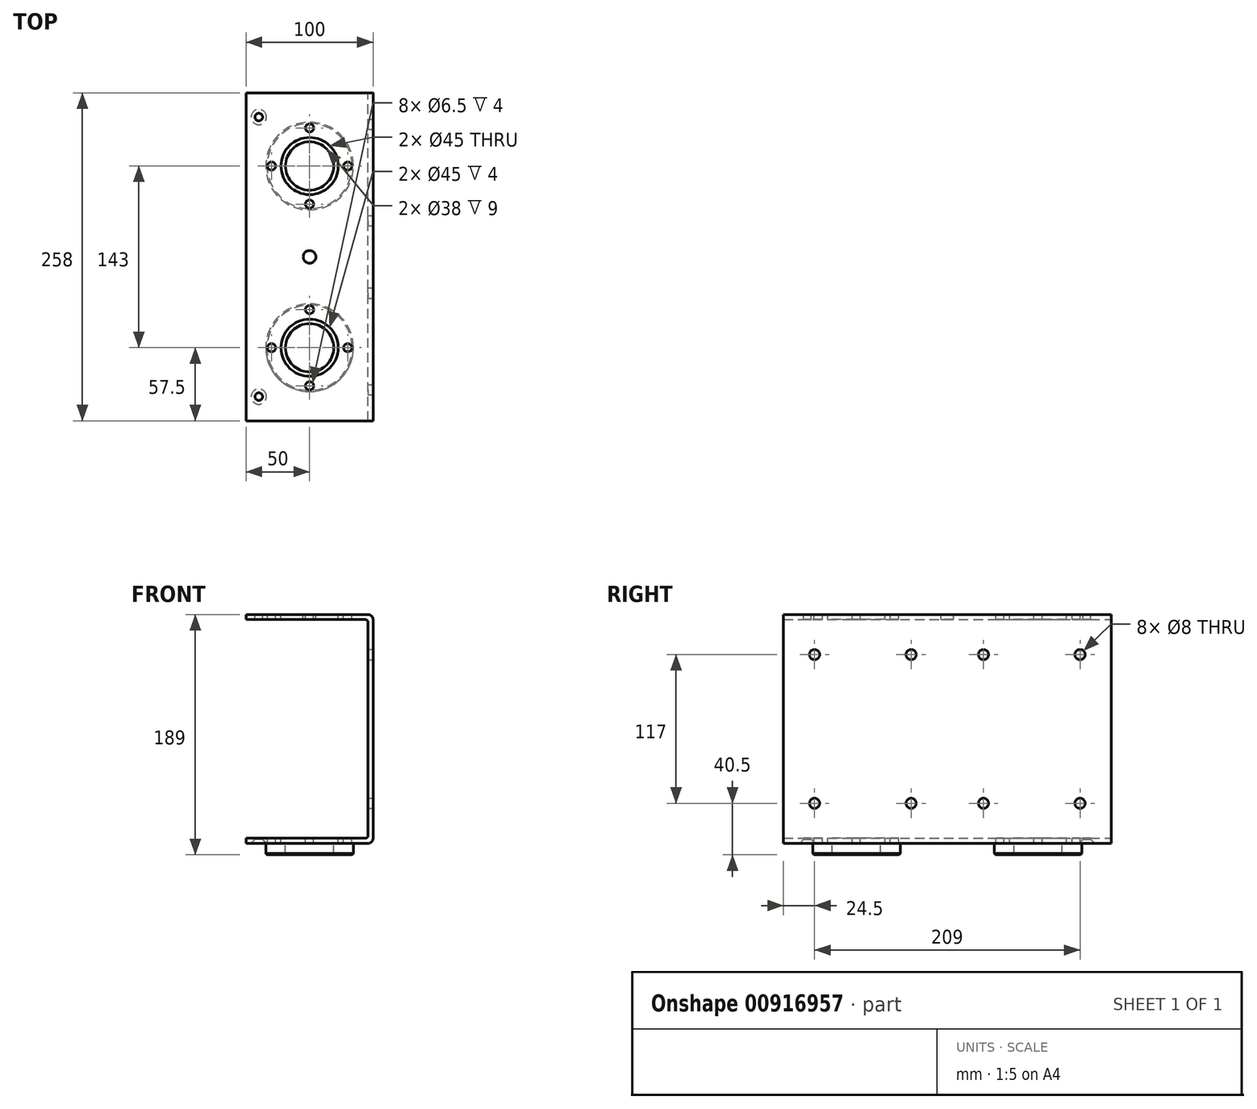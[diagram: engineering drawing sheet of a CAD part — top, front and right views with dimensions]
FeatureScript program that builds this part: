
annotation { "Feature Type Name" : "Feature", "Feature Type Description" : "" }
export const myFeature = defineFeature(function(context is Context, id is Id, definition is map)
    precondition{}
    {
        {
            var Q0;
            Q0=qCreatedBy(makeId("Front.planeOp"),FACE);
            var sketch = newSketch(context, id + "F0", { "sketchPlane" : qUnion([Q0])});
            skLineSegment(sketch, "E0.bottom", {"start": v(0, 0) * mm, "end": v(96, 0) * mm});
            skLineSegment(sketch, "E0.top", {"start": v(0, 180) * mm, "end": v(96, 180) * mm});
            skLineSegment(sketch, "E0.left", {"start": v(0, 0) * mm, "end": v(0, 4) * mm});
            skLineSegment(sketch, "E0.right", {"start": v(100, 4) * mm, "end": v(100, 176) * mm});
            skLineSegment(sketch, "E1.0", {"start": v(0, 176) * mm, "end": v(94, 176) * mm});
            skLineSegment(sketch, "E2.0", {"start": v(96, 6) * mm, "end": v(96, 174) * mm});
            skLineSegment(sketch, "E3.0", {"start": v(0, 4) * mm, "end": v(94, 4) * mm});
            skLineSegment(sketch, "E4.trimOffspring", {"start": v(0, 176) * mm, "end": v(0, 180) * mm});
            skPoint(sketch, "E5.visualSharp", {"position": v(100, 180) * mm});
            skArc(sketch, "E5.filletArc", {"start": v(100, 176) * mm, "mid": v(98.83, 178.83) * mm, "end": v(96, 180) * mm});
            skArc(sketch, "E6.filletArc", {"start": v(96, 174) * mm, "mid": v(95.41, 175.41) * mm, "end": v(94, 176) * mm});
            skPoint(sketch, "E7.visualSharp", {"position": v(96, 4) * mm});
            skArc(sketch, "E7.filletArc", {"start": v(94, 4) * mm, "mid": v(95.41, 4.59) * mm, "end": v(96, 6) * mm});
            skPoint(sketch, "E8.visualSharp", {"position": v(100, 0) * mm});
            skArc(sketch, "E8.filletArc", {"start": v(96, 0) * mm, "mid": v(98.83, 1.17) * mm, "end": v(100, 4) * mm});
            skSolve(sketch);
        }
        {
            var Q0;
            Q0=qSketchRegion(id+"F0",true);
            extrude(context, id + "F1", {"entities" : qUnion([Q0]), "depth" : 258 * mm, "offsetDistance" : 25 * mm});
        }
        {
            var Q0;
            Q0=makeQuery(id+"F1.opExtrude","SWEPT_FACE",FACE,{"disambiguationData":[OSD([sQuery(id+"F0.wireOp",EDGE,"E0.top")])]});
            var sketch = newSketch(context, id + "F2", { "sketchPlane" : qUnion([Q0])});
            skCircle(sketch, "E9", {"center": v(50, -200.5) * mm, "radius": 22.5 * mm});
            skCircle(sketch, "E10", {"center": v(50, -57.5) * mm, "radius": 22.5 * mm});
            skCircle(sketch, "E11", {"center": v(50, -129) * mm, "radius": 5 * mm});
            skPoint(sketch, "E11.centerSnap0", {"position": v(0, -129) * mm});
            skCircle(sketch, "E12", {"center": v(50, -200.5) * mm, "radius": 30 * mm, "construction": true});
            skCircle(sketch, "E13", {"center": v(20, -200.5) * mm, "radius": 3.25 * mm});
            skCircle(sketch, "E14", {"center": v(80, -200.5) * mm, "radius": 3.25 * mm});
            skCircle(sketch, "E15", {"center": v(50, -170.5) * mm, "radius": 3.25 * mm});
            skCircle(sketch, "E16", {"center": v(50, -230.5) * mm, "radius": 3.25 * mm});
            skCircle(sketch, "E17.0.1.0", {"center": v(80, -57.5) * mm, "radius": 3.25 * mm});
            skCircle(sketch, "E17.0.1.1", {"center": v(50, -27.5) * mm, "radius": 3.25 * mm});
            skCircle(sketch, "E17.0.1.2", {"center": v(20, -57.5) * mm, "radius": 3.25 * mm});
            skCircle(sketch, "E17.0.1.3", {"center": v(50, -87.5) * mm, "radius": 3.25 * mm});
            skLineSegment(sketch, "E17.direction1", {"start": v(80, -200.5) * mm, "end": v(105, -200.5) * mm, "construction": true});
            skLineSegment(sketch, "E17.direction2", {"start": v(80, -200.5) * mm, "end": v(80, -57.5) * mm, "construction": true});
            skSolve(sketch);
        }
        {
            var Q0;
            Q0=makeQuery(id+"F2.imprint","IMPRINT",FACE,{"disambiguationData":[TD([[makeQuery(id+"F2.imprint","IMPRINT",EDGE,{"derivedFrom":sQuery(id+"F2.wireOp",EDGE,"E9")}),1.0]])]});
            var Q1;
            Q1=makeQuery(id+"F2.imprint","IMPRINT",FACE,{"disambiguationData":[TD([[makeQuery(id+"F2.imprint","IMPRINT",EDGE,{"derivedFrom":sQuery(id+"F2.wireOp",EDGE,"E17.0.1.3")}),1.0]])]});
            var Q2;
            Q2=makeQuery(id+"F2.imprint","IMPRINT",FACE,{"disambiguationData":[TD([[makeQuery(id+"F2.imprint","IMPRINT",EDGE,{"derivedFrom":sQuery(id+"F2.wireOp",EDGE,"E10")}),1.0]])]});
            var Q3;
            Q3=makeQuery(id+"F2.imprint","IMPRINT",FACE,{"disambiguationData":[TD([[makeQuery(id+"F2.imprint","IMPRINT",EDGE,{"derivedFrom":sQuery(id+"F2.wireOp",EDGE,"E17.0.1.2")}),1.0]])]});
            var Q4;
            Q4=makeQuery(id+"F2.imprint","IMPRINT",FACE,{"disambiguationData":[TD([[makeQuery(id+"F2.imprint","IMPRINT",EDGE,{"derivedFrom":sQuery(id+"F2.wireOp",EDGE,"E17.0.1.0")}),1.0]])]});
            var Q5;
            Q5=makeQuery(id+"F2.imprint","IMPRINT",FACE,{"disambiguationData":[TD([[makeQuery(id+"F2.imprint","IMPRINT",EDGE,{"derivedFrom":sQuery(id+"F2.wireOp",EDGE,"E17.0.1.1")}),1.0]])]});
            var Q6;
            Q6=makeQuery(id+"F2.imprint","IMPRINT",FACE,{"disambiguationData":[TD([[makeQuery(id+"F2.imprint","IMPRINT",EDGE,{"derivedFrom":sQuery(id+"F2.wireOp",EDGE,"E15")}),1.0]])]});
            var Q7;
            Q7=makeQuery(id+"F2.imprint","IMPRINT",FACE,{"disambiguationData":[TD([[makeQuery(id+"F2.imprint","IMPRINT",EDGE,{"derivedFrom":sQuery(id+"F2.wireOp",EDGE,"E14")}),1.0]])]});
            var Q8;
            Q8=makeQuery(id+"F2.imprint","IMPRINT",FACE,{"disambiguationData":[TD([[makeQuery(id+"F2.imprint","IMPRINT",EDGE,{"derivedFrom":sQuery(id+"F2.wireOp",EDGE,"E16")}),1.0]])]});
            var Q9;
            Q9=makeQuery(id+"F2.imprint","IMPRINT",FACE,{"disambiguationData":[TD([[makeQuery(id+"F2.imprint","IMPRINT",EDGE,{"derivedFrom":sQuery(id+"F2.wireOp",EDGE,"E13")}),1.0]])]});
            extrude(context, id + "F3", {"entities" : qUnion([Q0, Q1, Q2, Q3, Q4, Q5, Q6, Q7, Q8, Q9]), "operationType" : NewBodyOperationType.REMOVE, "endBound" : BoundingType.THROUGH_ALL, "oppositeDirection" : true, "depth" : 25 * mm, "offsetDistance" : 25 * mm});
        }
        {
            var Q0;
            Q0=makeQuery(id+"F2.imprint","IMPRINT",FACE,{"disambiguationData":[TD([[makeQuery(id+"F2.imprint","IMPRINT",EDGE,{"derivedFrom":sQuery(id+"F2.wireOp",EDGE,"E11")}),1.0]])]});
            extrude(context, id + "F4", {"entities" : qUnion([Q0]), "operationType" : NewBodyOperationType.REMOVE, "endBound" : BoundingType.UP_TO_NEXT, "oppositeDirection" : true, "depth" : 25 * mm, "offsetDistance" : 25 * mm});
        }
        {
            var Q0;
            Q0=makeQuery(id+"F1.opExtrude","SWEPT_FACE",FACE,{"disambiguationData":[OSD([sQuery(id+"F0.wireOp",EDGE,"E0.right")])]});
            var sketch = newSketch(context, id + "F5", { "sketchPlane" : qUnion([Q0])});
            skCircle(sketch, "E18", {"center": v(-233.5, 148.5) * mm, "radius": 4 * mm});
            skCircle(sketch, "E19.0.1.0", {"center": v(-233.5, 31.5) * mm, "radius": 4 * mm});
            skCircle(sketch, "E19.1.0.0", {"center": v(-157.5, 148.5) * mm, "radius": 4 * mm});
            skCircle(sketch, "E19.1.1.0", {"center": v(-157.5, 31.5) * mm, "radius": 4 * mm});
            skLineSegment(sketch, "E19.direction1", {"start": v(-233.5, 148.5) * mm, "end": v(-157.5, 148.5) * mm, "construction": true});
            skLineSegment(sketch, "E19.direction2", {"start": v(-233.5, 148.5) * mm, "end": v(-233.5, 31.5) * mm, "construction": true});
            skLineSegment(sketch, "E20", {"start": v(-129, 176) * mm, "end": v(-129, 155.07) * mm, "construction": true});
            skCircle(sketch, "E21.MirrorC", {"center": v(-100.5, 148.5) * mm, "radius": 4 * mm});
            skCircle(sketch, "E22.MirrorC", {"center": v(-100.5, 31.5) * mm, "radius": 4 * mm});
            skCircle(sketch, "E23.MirrorC", {"center": v(-24.5, 148.5) * mm, "radius": 4 * mm});
            skCircle(sketch, "E24.MirrorC", {"center": v(-24.5, 31.5) * mm, "radius": 4 * mm});
            skSolve(sketch);
        }
        {
            var Q0;
            Q0=qSketchRegion(id+"F5",true);
            extrude(context, id + "F6", {"entities" : qUnion([Q0]), "operationType" : NewBodyOperationType.REMOVE, "endBound" : BoundingType.THROUGH_ALL, "oppositeDirection" : true, "depth" : 25 * mm, "offsetDistance" : 25 * mm});
        }
        {
            var Q0;
            Q0=makeQuery(id+"F1.opExtrude","SWEPT_FACE",FACE,{"disambiguationData":[OSD([sQuery(id+"F0.wireOp",EDGE,"E0.top")])]});
            var sketch = newSketch(context, id + "F7", { "sketchPlane" : qUnion([Q0])});
            skCircle(sketch, "E25", {"center": v(10, -239) * mm, "radius": 3 * mm});
            skLineSegment(sketch, "E26", {"start": v(0, -129) * mm, "end": v(-19.63, -129) * mm, "construction": true});
            skCircle(sketch, "E27.MirrorC", {"center": v(10, -19) * mm, "radius": 3 * mm});
            skSolve(sketch);
        }
        {
            var Q0;
            Q0=qSketchRegion(id+"F7",true);
            extrude(context, id + "F8", {"entities" : qUnion([Q0]), "operationType" : NewBodyOperationType.REMOVE, "endBound" : BoundingType.THROUGH_ALL, "oppositeDirection" : true, "depth" : 25 * mm, "offsetDistance" : 25 * mm});
        }
        {
            var Q0;
            Q0=makeQuery(id+"F8.boolean.opBoolean","COPY",EDGE,{"derivedFrom":makeQuery(id+"F8.opExtrude","CAP_EDGE",EDGE,{"disambiguationData":[OSD([sQuery(id+"F7.wireOp",EDGE,"E27.MirrorC")])],"isStart":true})});
            var Q1;
            Q1=makeQuery(id+"F8.boolean.opBoolean","COPY",EDGE,{"derivedFrom":makeQuery(id+"F8.opExtrude","CAP_EDGE",EDGE,{"disambiguationData":[OSD([sQuery(id+"F7.wireOp",EDGE,"E25")])],"isStart":true})});
            var Q2;
            Q2=makeQuery(id+"F8.boolean.opBoolean","INTERSECT",EDGE,{"derivedFrom":[makeQuery(id+"F1.opExtrude","SWEPT_FACE",FACE,{"disambiguationData":[OSD([sQuery(id+"F0.wireOp",EDGE,"E0.bottom")])]}),makeQuery(id+"F8.opExtrude","SWEPT_FACE",FACE,{"disambiguationData":[OSD([sQuery(id+"F7.wireOp",EDGE,"E25")])]})]});
            var Q3;
            Q3=makeQuery(id+"F8.boolean.opBoolean","INTERSECT",EDGE,{"derivedFrom":[makeQuery(id+"F1.opExtrude","SWEPT_FACE",FACE,{"disambiguationData":[OSD([sQuery(id+"F0.wireOp",EDGE,"E0.bottom")])]}),makeQuery(id+"F8.opExtrude","SWEPT_FACE",FACE,{"disambiguationData":[OSD([sQuery(id+"F7.wireOp",EDGE,"E27.MirrorC")])]})]});
            chamfer(context, id + "F9", {"entities" : qUnion([Q0, Q1, Q2, Q3]), "chamferType" : ChamferType.TWO_OFFSETS, "width1" : 3 * mm, "oppositeDirection" : false, "width2" : 3 * mm, "tangentPropagation" : true});
        }
        {
            var Q0;
            Q0=makeQuery(id+"F1.opExtrude","SWEPT_FACE",FACE,{"disambiguationData":[OSD([sQuery(id+"F0.wireOp",EDGE,"E0.bottom")])]});
            var sketch = newSketch(context, id + "F10", { "sketchPlane" : qUnion([Q0])});
            skCircle(sketch, "E28", {"center": v(50, 57.5) * mm, "radius": 34.5 * mm});
            skCircle(sketch, "E29", {"center": v(50, 200.5) * mm, "radius": 34.5 * mm});
            skCircle(sketch, "E30", {"center": v(50, 200.5) * mm, "radius": 19 * mm});
            skCircle(sketch, "E31", {"center": v(50, 57.5) * mm, "radius": 19 * mm});
            skSolve(sketch);
        }
        {
            var Q0;
            Q0=qSketchRegion(id+"F10",true);
            extrude(context, id + "F11", {"entities" : qUnion([Q0]), "operationType" : NewBodyOperationType.ADD, "depth" : 9 * mm, "offsetDistance" : 25 * mm});
        }
        {
            var Q0;
            Q0=makeQuery(id+"F11.opExtrude","CAP_EDGE",EDGE,{"disambiguationData":[OSD([sQuery(id+"F10.wireOp",EDGE,"E29")])],"isStart":false});
            var Q1;
            Q1=makeQuery(id+"F11.opExtrude","CAP_EDGE",EDGE,{"disambiguationData":[OSD([sQuery(id+"F10.wireOp",EDGE,"E28")])],"isStart":false});
            chamfer(context, id + "F12", {"entities" : qUnion([Q0, Q1]), "width" : 1 * mm, "tangentPropagation" : true});
        }
    });
